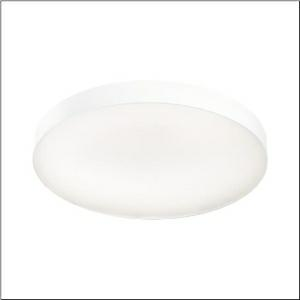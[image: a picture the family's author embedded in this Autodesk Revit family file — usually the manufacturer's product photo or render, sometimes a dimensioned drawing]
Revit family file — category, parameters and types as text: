
# Revit family: round_21_l_51mr38nd0321w
name_source: partatom
category: Lighting Fixtures
units: mm (PartAtom-declared; Revit-internal decimal feet)

## family parameters
Cut with Voids When Loaded = No
Host = Face
Light Source = No
Part Type = Normal
Room Calculation Point = No
Round Connector Dimension = Use Diameter
Shared = No

## types (1)
- Round 21 L (1 x LED, 11740 lm, 88.2 W, 3000K)
    Apparent Load = 88 VA
    CIE Flux Codes = 66 90 98 71 100
    Color Rendering = 80
    Color Temperature = 3000K
    Default Elevation = 1800 mm
    Description = Round 21 L, wall and ceiling luminaire, primary optical cover: micro prismatic cover, of PMMA, transparent, CAT 2 (L<= 3000cd/m²), light emission: direct/indirect distribution, primary light characteristic: symmetric, installation type: suspended mounting, surface-mounted, LED, rated luminous flux: 11.740lm, luminous efficacy: 133lm/W, light colour: 830, colour temperature: 3000K, control gear: DALI 2, with terminal, 5-pole, mains connection: 230V, AC, 50/60Hz, rated input power: 88.2W, housing, of aluminium, coated, white, diameter: 850mm, height: 62mm, protection rating (complete): IP40, insulation class (complete): insulation class I (protective earthing), certification: CE, impact resistance: IK04, permissible operating ambient temperature: -10..+35°C, packaging unit: 1 piece
    Height = 87 mm
    Lamp = 1 x LED
    Lamp Light Flux = 11740 lm
    Lamp Power = 88.2 W
    Lamp count = 1
    Length = 850 mm
    Luminous efficacy = 133 lm/W
    Manufacturer = Siteco
    ModVariant = No
    Model = 51MR38ND0321W
    Mounting Place = Ceiling
    Mounting Type = Surface mounted
    Number of Poles = 1
    OnlyDefault = Yes
    Power Factor = 1
    Product Name = Round 21 L
    Product group = wall and ceiling luminaire
    ProductGroupID = 304
    Protection Class = Protection class I
    Protection Degree = IP 40
    RLX_Detail_Level = 1
    RLX_Emergency_Light_Flux = 0 lm
    RLX_Emergency_Type = 0
    RLX_Emergency_Type_DB = No
    RlxData = <blob elided: 19529 chars, md5=dd8f521c>
    Socket = socket
    Standby Power = 0 W
    System Light Flux = 11740 lm
    System Power = 88 W
    Type Comments = Product without accessories
    Type Image = l_1258318.jpg
    URL = http://relux.com
    VarID = ---
    Voltage = 0 V
    Weight = 0.00 kg
    Width = 0 mm  [stored 0 ft]

note: [stored X ft] marks values corroborated as IEEE doubles in the binary element streams (Revit-internal decimal feet)

## geometry (parser evidence)
native form markers: Blend x4, Sweep x11
no freeform markers — native parametric forms only
